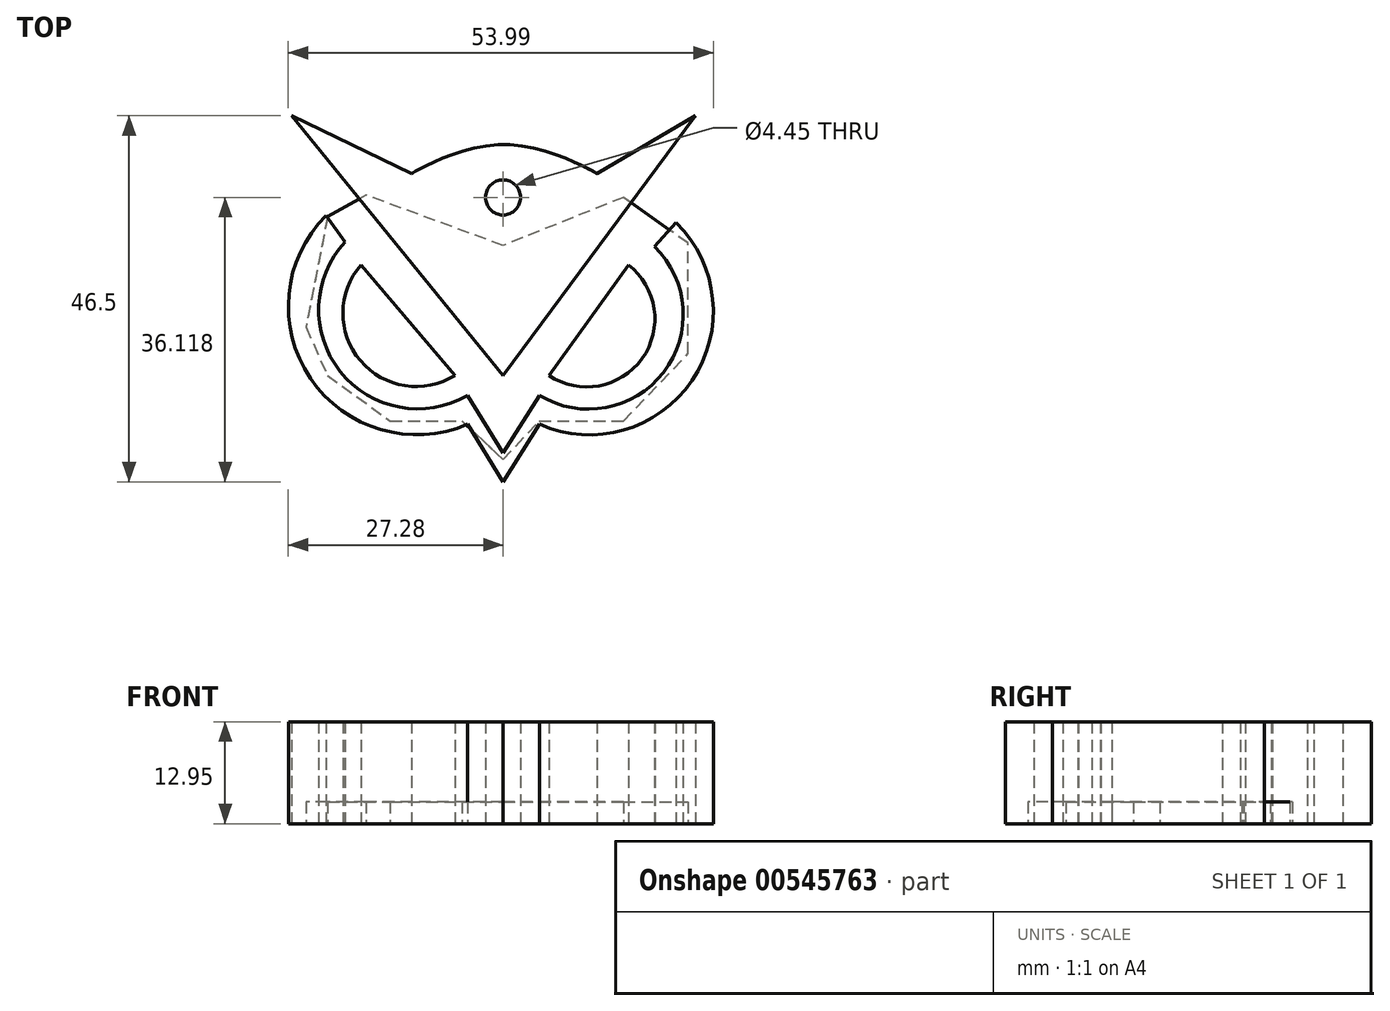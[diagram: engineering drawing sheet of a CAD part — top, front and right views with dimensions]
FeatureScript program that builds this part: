
annotation { "Feature Type Name" : "Feature", "Feature Type Description" : "" }
export const myFeature = defineFeature(function(context is Context, id is Id, definition is map)
    precondition{}
    {
        {
            var Q0;
            Q0=qCreatedBy(makeId("Top.planeOp"),FACE);
            var sketch = newSketch(context, id + "F0", { "sketchPlane" : qUnion([Q0])});
            skLineSegment(sketch, "E0", {"start": v(-26.87, 32.98) * mm, "end": v(0, 0) * mm});
            skLineSegment(sketch, "E1", {"start": v(0, 0) * mm, "end": v(24.43, 32.98) * mm});
            skLineSegment(sketch, "E2", {"start": v(24.43, 32.98) * mm, "end": v(11.9, 25.65) * mm});
            skFitSpline(sketch, "E3", {"points": [v(11.9, 25.65) * mm, v(0, 29.32) * mm, v(-11.6, 25.65) * mm, v(0, 29.63) * mm, v(11.9, 25.65) * mm]});
            skLineSegment(sketch, "E4", {"start": v(-26.87, 32.98) * mm, "end": v(-11.6, 25.65) * mm});
            skCircle(sketch, "E5", {"center": v(0, 22.6) * mm, "radius": 2.22 * mm});
            skSolve(sketch);
        }
        {
            var Q0;
            Q0=qCreatedBy(makeId("Top.planeOp"),FACE);
            var sketch = newSketch(context, id + "F1", { "sketchPlane" : qUnion([Q0])});
            skLineSegment(sketch, "E6", {"start": v(5.82, 0) * mm, "end": v(15.9, 14.04) * mm});
            skLineSegment(sketch, "E7", {"start": v(-6.1, 0) * mm, "end": v(-18.02, 14.04) * mm});
            skArc(sketch, "E8", {"start": v(-18.02, 14.04) * mm, "mid": v(-18.13, 1.87) * mm, "end": v(-6.1, 0) * mm});
            skArc(sketch, "E9", {"start": v(5.82, 0) * mm, "mid": v(17.66, 2.13) * mm, "end": v(15.9, 14.04) * mm});
            skSolve(sketch);
        }
        {
            var Q0;
            Q0=qCreatedBy(makeId("Top.planeOp"),FACE);
            var sketch = newSketch(context, id + "F2", { "sketchPlane" : qUnion([Q0])});
            skArc(sketch, "E10", {"start": v(4.63, -2.56) * mm, "mid": v(20.37, 0.36) * mm, "end": v(19.25, 16.33) * mm});
            skArc(sketch, "E11", {"start": v(-20.05, 16.94) * mm, "mid": v(-20.68, 0.5) * mm, "end": v(-4.51, -2.56) * mm});
            skLineSegment(sketch, "E12", {"start": v(-4.51, -2.56) * mm, "end": v(0, -9.87) * mm});
            skLineSegment(sketch, "E13", {"start": v(0, -9.87) * mm, "end": v(4.63, -2.56) * mm});
            skLineSegment(sketch, "E14", {"start": v(-20.05, 16.94) * mm, "end": v(-22.49, 20.3) * mm});
            skLineSegment(sketch, "E15", {"start": v(19.25, 16.33) * mm, "end": v(22, 19.38) * mm});
            skArc(sketch, "E16", {"start": v(4.63, -6.21) * mm, "mid": v(24, -0.67) * mm, "end": v(22, 19.38) * mm});
            skPoint(sketch, "E16.startSnap0", {"position": v(2.31, -6.21) * mm});
            skArc(sketch, "E17", {"start": v(-22.49, 20.3) * mm, "mid": v(-24.47, -0.4) * mm, "end": v(-4.51, -6.21) * mm});
            skLineSegment(sketch, "E18", {"start": v(-4.51, -6.21) * mm, "end": v(0, -13.52) * mm});
            skLineSegment(sketch, "E19", {"start": v(0, -13.52) * mm, "end": v(4.63, -6.21) * mm});
            skSolve(sketch);
        }
        {
            var Q0;
            Q0=makeQuery(id+"F0.imprint","IMPRINT",FACE,{"disambiguationData":[TD([[makeQuery(id+"F0.imprint","IMPRINT",EDGE,{"derivedFrom":sQuery(id+"F0.wireOp",EDGE,"E0")}),1.0]])]});
            var Q1;
            Q1=makeQuery(id+"F1.imprint","IMPRINT",FACE,{"disambiguationData":[TD([[makeQuery(id+"F1.imprint","IMPRINT",EDGE,{"derivedFrom":sQuery(id+"F1.wireOp",EDGE,"E7")}),1.0]])]});
            var Q2;
            Q2=makeQuery(id+"F2.imprint","IMPRINT",FACE,{"disambiguationData":[TD([[makeQuery(id+"F2.imprint","IMPRINT",EDGE,{"derivedFrom":sQuery(id+"F2.wireOp",EDGE,"E10")}),-1.0]])]});
            var Q3;
            Q3=makeQuery(id+"F1.imprint","IMPRINT",FACE,{"disambiguationData":[TD([[makeQuery(id+"F1.imprint","IMPRINT",EDGE,{"derivedFrom":sQuery(id+"F1.wireOp",EDGE,"E6")}),-1.0]])]});
            extrude(context, id + "F3", {"entities" : qUnion([Q0, Q1, Q2, Q3]), "depth" : 12.95 * mm, "offsetDistance" : 25.4 * mm});
        }
        {
            var Q0;
            Q0=qCreatedBy(makeId("Top.planeOp"),FACE);
            var sketch = newSketch(context, id + "F4", { "sketchPlane" : qUnion([Q0])});
            skLineSegment(sketch, "E20", {"start": v(-17.4, 22.9) * mm, "end": v(-22.3, 20.16) * mm});
            skLineSegment(sketch, "E21", {"start": v(-22.3, 20.16) * mm, "end": v(-25.04, 6.1) * mm});
            skLineSegment(sketch, "E22", {"start": v(-25.04, 6.1) * mm, "end": v(-22.3, 0) * mm});
            skLineSegment(sketch, "E23", {"start": v(-22.3, 0) * mm, "end": v(-14.35, -5.8) * mm});
            skLineSegment(sketch, "E24", {"start": v(-14.35, -5.8) * mm, "end": v(-5.2, -5.8) * mm});
            skLineSegment(sketch, "E25", {"start": v(-5.2, -5.8) * mm, "end": v(0, -10.69) * mm});
            skLineSegment(sketch, "E26", {"start": v(0, -10.69) * mm, "end": v(4.6, -5.8) * mm});
            skLineSegment(sketch, "E27", {"start": v(4.6, -5.8) * mm, "end": v(15.27, -5.8) * mm});
            skLineSegment(sketch, "E28", {"start": v(15.27, -5.8) * mm, "end": v(23.51, 2.75) * mm});
            skLineSegment(sketch, "E29", {"start": v(23.51, 2.75) * mm, "end": v(23.51, 12.22) * mm});
            skLineSegment(sketch, "E30", {"start": v(23.51, 12.22) * mm, "end": v(23.51, 16.8) * mm});
            skLineSegment(sketch, "E31", {"start": v(23.51, 16.8) * mm, "end": v(15.27, 22.6) * mm});
            skLineSegment(sketch, "E32", {"start": v(15.27, 22.6) * mm, "end": v(0, 16.5) * mm});
            skLineSegment(sketch, "E33", {"start": v(0, 16.5) * mm, "end": v(-17.4, 22.9) * mm});
            skSolve(sketch);
        }
        {
            var Q0;
            Q0 = qSketchRegion(id + "F4", true);
            extrude(context, id + "F5", {"entities" : qUnion([Q0]), "depth" : 2.8 * mm, "offsetDistance" : 25.4 * mm});
        }
    });
